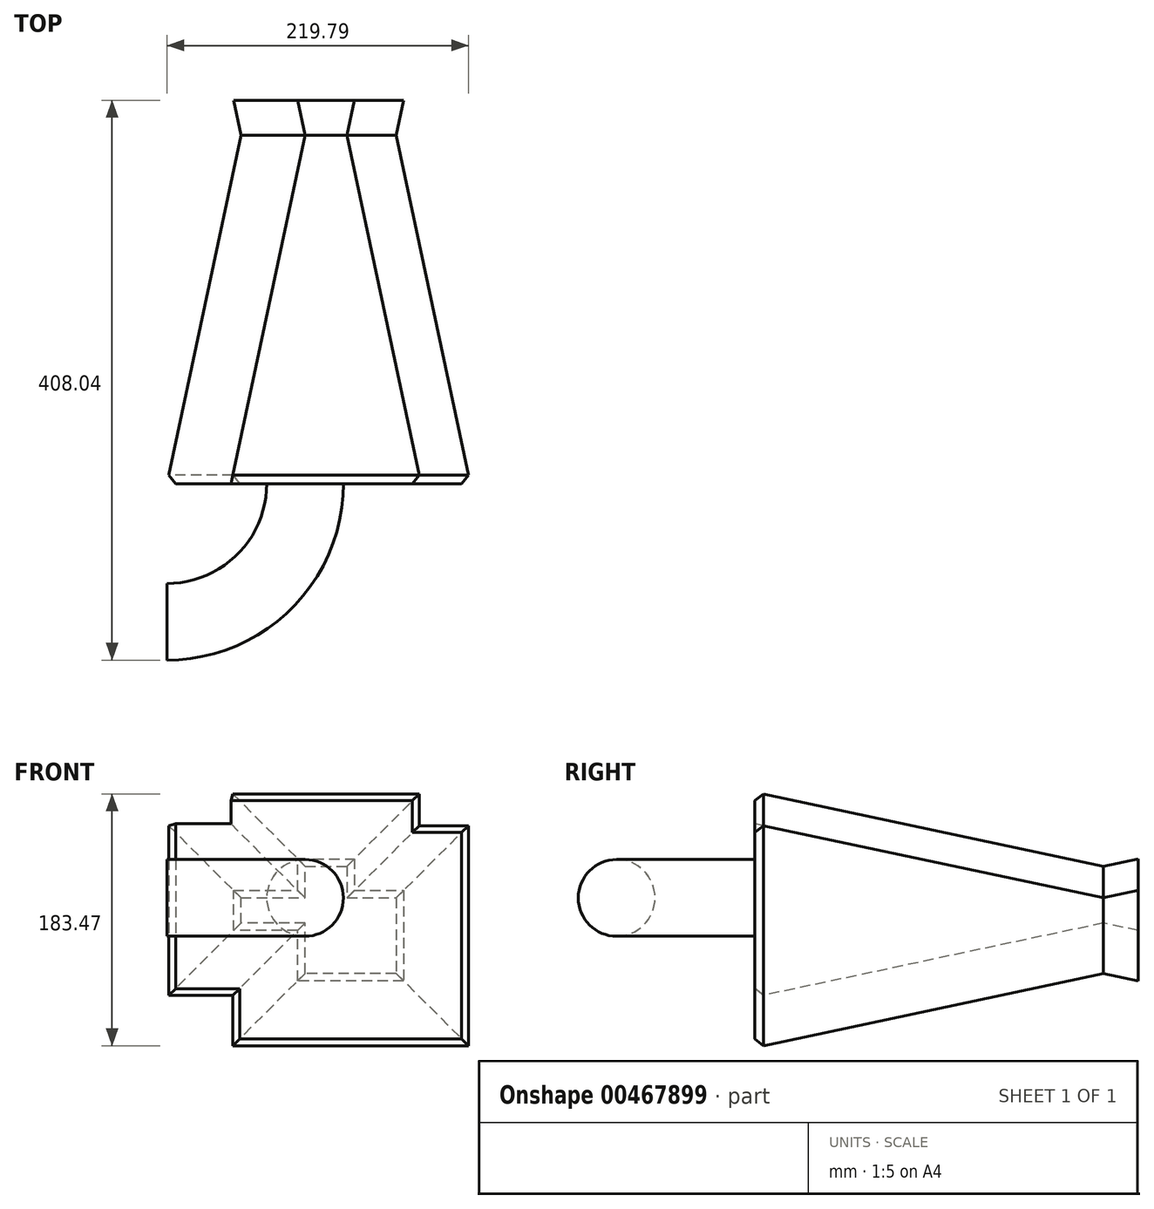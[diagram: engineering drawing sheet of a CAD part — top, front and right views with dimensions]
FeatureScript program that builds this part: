
annotation { "Feature Type Name" : "Feature", "Feature Type Description" : "" }
export const myFeature = defineFeature(function(context is Context, id is Id, definition is map)
    precondition{}
    {
        {
            var Q0;
            Q0=qCreatedBy(makeId("Front.planeOp"),FACE);
            var sketch = newSketch(context, id + "F0", { "sketchPlane" : qUnion([Q0])});
            skLineSegment(sketch, "E0.bottom", {"start": v(0, 0) * mm, "end": v(30.57, 0) * mm});
            skLineSegment(sketch, "E0.top", {"start": v(0, 23.11) * mm, "end": v(30.57, 23.11) * mm});
            skLineSegment(sketch, "E0.left", {"start": v(0, 0) * mm, "end": v(0, 23.11) * mm});
            skLineSegment(sketch, "E0.right", {"start": v(30.57, 0) * mm, "end": v(30.57, 23.11) * mm});
            skLineSegment(sketch, "E1.bottom", {"start": v(0, 0) * mm, "end": v(-46.7, 0) * mm});
            skLineSegment(sketch, "E1.top", {"start": v(0, -18.33) * mm, "end": v(-46.7, -18.33) * mm});
            skLineSegment(sketch, "E1.left", {"start": v(0, 0) * mm, "end": v(0, -18.33) * mm});
            skLineSegment(sketch, "E1.right", {"start": v(-46.7, 0) * mm, "end": v(-46.7, -18.33) * mm});
            skLineSegment(sketch, "E2.bottom", {"start": v(0, 0) * mm, "end": v(-40.28, 0) * mm});
            skLineSegment(sketch, "E2.top", {"start": v(0, 39.94) * mm, "end": v(-40.28, 39.94) * mm});
            skLineSegment(sketch, "E2.left", {"start": v(0, 0) * mm, "end": v(0, 39.94) * mm});
            skLineSegment(sketch, "E2.right", {"start": v(-40.28, 0) * mm, "end": v(-40.28, 39.94) * mm});
            skLineSegment(sketch, "E3.bottom", {"start": v(0, 0) * mm, "end": v(66.4, 0) * mm});
            skLineSegment(sketch, "E3.top", {"start": v(0, -54.98) * mm, "end": v(66.4, -54.98) * mm});
            skLineSegment(sketch, "E3.left", {"start": v(0, 0) * mm, "end": v(0, -54.98) * mm});
            skLineSegment(sketch, "E3.right", {"start": v(66.4, 0) * mm, "end": v(66.4, -54.98) * mm});
            skSolve(sketch);
        }
        {
            var Q0;
            {var subQ0=sQuery(id+"F0.wireOp",EDGE,"E0.top");Q0=makeQuery(id+"F0.imprint","IMPRINT",FACE,{"disambiguationData":[TD([[makeQuery(id+"F0.imprint","IMPRINT",EDGE,{"derivedFrom":subQ0}),-1.0]])]});}
            var Q1;
            {var subQ4=sQuery(id+"F0.wireOp",EDGE,"E3.top");Q1=makeQuery(id+"F0.imprint","IMPRINT",FACE,{"disambiguationData":[TD([[makeQuery(id+"F0.imprint","IMPRINT",EDGE,{"derivedFrom":subQ4}),1.0]])]});}
            var Q2;
            Q2=makeQuery(id+"F0.imprint","IMPRINT",FACE,{"disambiguationData":[TD([[makeQuery(id+"F0.imprint","IMPRINT",EDGE,{"derivedFrom":sQuery(id+"F0.wireOp",EDGE,"E1.bottom")}),1.0]])]});
            var Q3;
            {var subQ3=sQuery(id+"F0.wireOp",EDGE,"E2.bottom");Q3=makeQuery(id+"F0.imprint","IMPRINT",FACE,{"disambiguationData":[TD([[makeQuery(id+"F0.imprint","IMPRINT",EDGE,{"derivedFrom":subQ3}),-1.0]])]});}
            extrude(context, id + "F1", {"entities" : qUnion([Q0, Q1, Q2, Q3]), "depth" : 254 * mm, "hasDraft" : true, "draftAngle" : 12 * degree, "hasSecondDirection" : true, "secondDirectionOppositeDirection" : true, "secondDirectionDepth" : 25.4 * mm, "hasSecondDirectionDraft" : true, "secondDirectionDraftAngle" : 12 * degree});
        }
        {
            var Q0;
            Q0=makeQuery(id+"F1.opExtrude","CAP_FACE",FACE,{"disambiguationData":[OSD([sQuery(id+"F0.wireOp",EDGE,"E0.top"),sQuery(id+"F0.wireOp",EDGE,"E0.right"),sQuery(id+"F0.wireOp",EDGE,"E1.bottom"),sQuery(id+"F0.wireOp",EDGE,"E1.top"),sQuery(id+"F0.wireOp",EDGE,"E1.right"),sQuery(id+"F0.wireOp",EDGE,"E2.top"),sQuery(id+"F0.wireOp",EDGE,"E2.left"),sQuery(id+"F0.wireOp",EDGE,"E2.right"),sQuery(id+"F0.wireOp",EDGE,"E3.bottom"),sQuery(id+"F0.wireOp",EDGE,"E3.top"),sQuery(id+"F0.wireOp",EDGE,"E3.left"),sQuery(id+"F0.wireOp",EDGE,"E3.right")])],"isStart":false});
            var sketch = newSketch(context, id + "F2", { "sketchPlane" : qUnion([Q0])});
            skCircle(sketch, "E4", {"center": v(0, 0) * mm, "radius": 27.94 * mm});
            skSolve(sketch);
        }
        {
            var Q0;
            Q0=makeQuery(id+"F2.imprint","IMPRINT",FACE,{"disambiguationData":[TD([[makeQuery(id+"F2.imprint","IMPRINT",EDGE,{"derivedFrom":sQuery(id+"F2.wireOp",EDGE,"E4")}),1.0]])]});
            var Q1;
            Q1=makeQuery(id+"F1.opExtrude","CAP_EDGE",EDGE,{"disambiguationData":[OSD([sQuery(id+"F0.wireOp",EDGE,"E1.right")])],"isStart":false});
            revolve(context, id + "F3", {"operationType" : NewBodyOperationType.ADD, "entities" : qUnion([Q0]), "axis" : qUnion([Q1]), "revolveType" : RevolveType.ONE_DIRECTION, "oppositeDirection" : true, "angle" : 90 * degree});
        }
        {
            var Q0;
            Q0=makeQuery(id+"F1.opExtrude","CAP_EDGE",EDGE,{"disambiguationData":[OSD([sQuery(id+"F0.wireOp",EDGE,"E1.top")])],"isStart":false});
            var Q1;
            Q1=makeQuery(id+"F1.opExtrude","CAP_EDGE",EDGE,{"disambiguationData":[OSD([sQuery(id+"F0.wireOp",EDGE,"E3.top")])],"isStart":false});
            var Q2;
            Q2=makeQuery(id+"F1.opExtrude","CAP_EDGE",EDGE,{"disambiguationData":[OSD([sQuery(id+"F0.wireOp",EDGE,"E1.right")])],"isStart":false});
            var Q3;
            Q3=makeQuery(id+"F1.opExtrude","CAP_EDGE",EDGE,{"disambiguationData":[OSD([sQuery(id+"F0.wireOp",EDGE,"E2.right")])],"isStart":false});
            var Q4;
            Q4=makeQuery(id+"F1.opExtrude","CAP_EDGE",EDGE,{"disambiguationData":[OSD([sQuery(id+"F0.wireOp",EDGE,"E3.right")])],"isStart":false});
            var Q5;
            Q5=makeQuery(id+"F1.opExtrude","CAP_EDGE",EDGE,{"disambiguationData":[OSD([sQuery(id+"F0.wireOp",EDGE,"E2.top")])],"isStart":false});
            var Q6;
            Q6=makeQuery(id+"F1.opExtrude","CAP_EDGE",EDGE,{"disambiguationData":[OSD([sQuery(id+"F0.wireOp",EDGE,"E2.left")])],"isStart":false});
            var Q7;
            Q7=makeQuery(id+"F1.opExtrude","CAP_EDGE",EDGE,{"disambiguationData":[OSD([sQuery(id+"F0.wireOp",EDGE,"E0.top")])],"isStart":false});
            var Q8;
            Q8=makeQuery(id+"F1.opExtrude","CAP_EDGE",EDGE,{"disambiguationData":[OSD([sQuery(id+"F0.wireOp",EDGE,"E0.right")])],"isStart":false});
            var Q9;
            Q9=makeQuery(id+"F1.opExtrude","CAP_EDGE",EDGE,{"disambiguationData":[OSD([sQuery(id+"F0.wireOp",EDGE,"E3.bottom")])],"isStart":false});
            var Q10;
            Q10=makeQuery(id+"F1.opExtrude","CAP_EDGE",EDGE,{"disambiguationData":[OSD([sQuery(id+"F0.wireOp",EDGE,"E3.left")])],"isStart":false});
            chamfer(context, id + "F4", {"entities" : qUnion([Q0, Q1, Q2, Q3, Q4, Q5, Q6, Q7, Q8, Q9, Q10]), "width" : 5.08 * mm, "tangentPropagation" : true});
        }
    });
